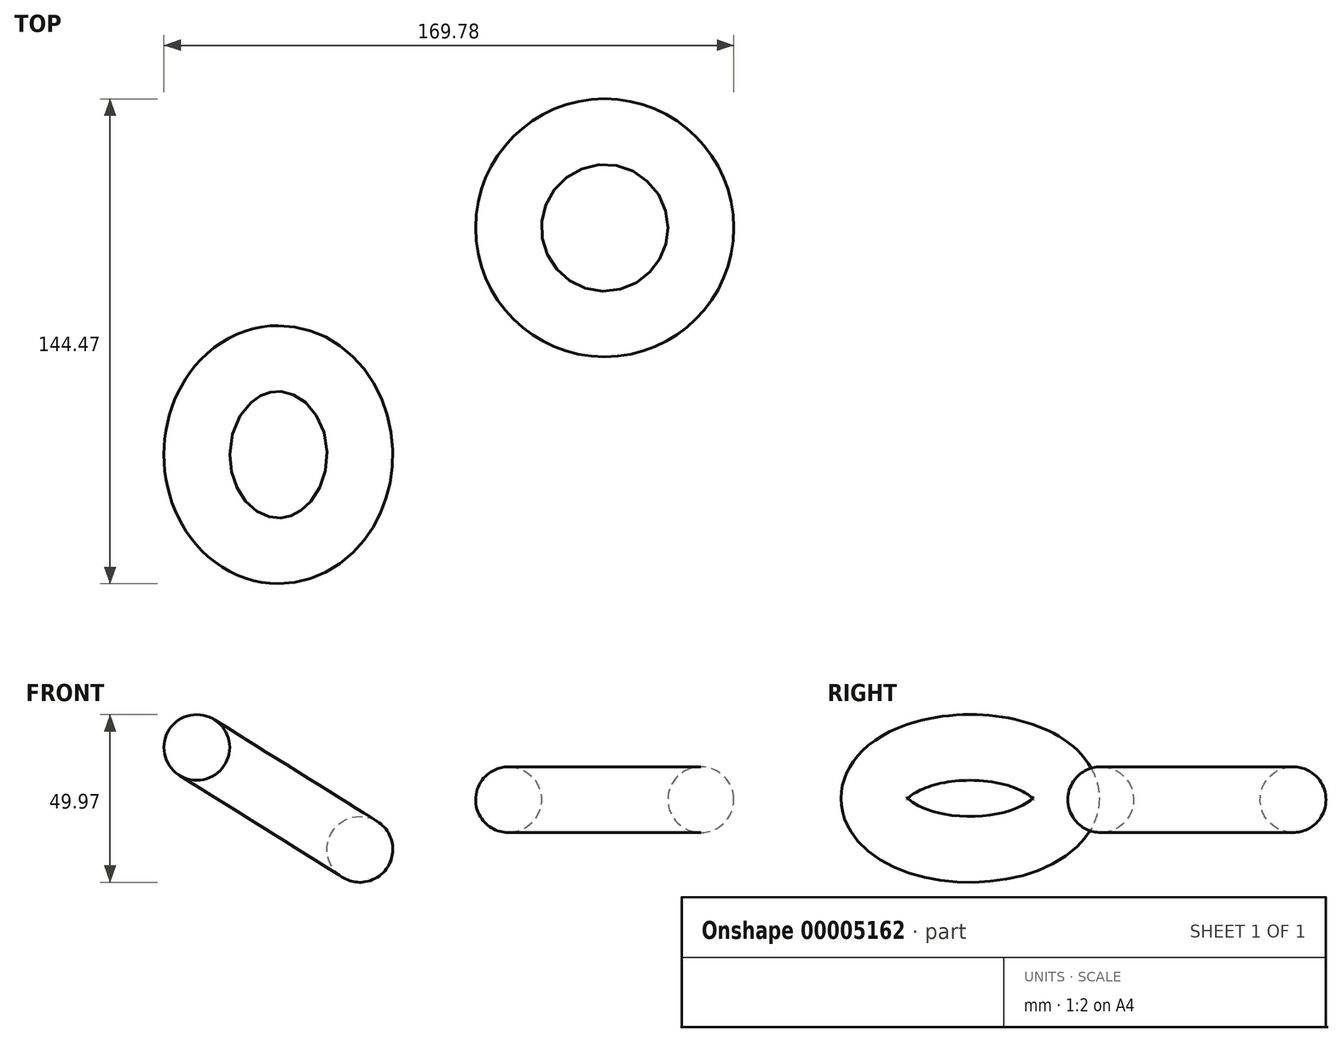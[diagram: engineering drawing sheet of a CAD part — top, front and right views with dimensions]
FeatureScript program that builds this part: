
annotation { "Feature Type Name" : "Feature", "Feature Type Description" : "" }
export const myFeature = defineFeature(function(context is Context, id is Id, definition is map)
    precondition{}
    {
        {
            var Q0;
            Q0=qCreatedBy(makeId("Front.planeOp"),FACE);
            var sketch = newSketch(context, id + "F0", { "sketchPlane" : qUnion([Q0])});
            skCircle(sketch, "E0", {"center": v(0, 0) * mm, "radius": 9.8 * mm});
            skLineSegment(sketch, "E1", {"start": v(-42.15, 28.65) * mm, "end": v(46.2, 28.65) * mm});
            skLineSegment(sketch, "E2", {"start": v(0, 28.65) * mm, "end": v(0, -9.8) * mm});
            skSolve(sketch);
        }
        {
            var Q0;
            Q0=makeQuery(id+"F0.imprint","IMPRINT",FACE,{"disambiguationData":[TD([[makeQuery(id+"F0.imprint","IMPRINT",EDGE,{"derivedFrom":sQuery(id+"F0.wireOp",EDGE,"E0")}),1.0]])]});
            var Q1;
            Q1=sQuery(id+"F0.wireOp",EDGE,"E1");
            revolve(context, id + "F1", {"entities" : qUnion([Q0]), "axis" : qUnion([Q1]), "revolveType" : RevolveType.FULL});
        }
        {
            var Q0;
            Q0=qCreatedBy(makeId("Right.planeOp"),FACE);
            var sketch = newSketch(context, id + "F2", { "sketchPlane" : qUnion([Q0])});
            skLineSegment(sketch, "E3.0", {"start": v(0, -9.8) * mm, "end": v(0, 9.8) * mm});
            skLineSegment(sketch, "E4", {"start": v(0, -9.8) * mm, "end": v(-30.29, -9.8) * mm});
            skSolve(sketch);
        }
        {
            var Q0;
            Q0=makeQuery(id+"F1.opRevolve","SWEPT_BODY",BODY,{"disambiguationData":[OSD([sQuery(id+"F0.wireOp",EDGE,"E0")])]});
            var Q1;
            Q1=sQuery(id+"F2.wireOp",EDGE,"E4");
            transform(context, id + "F3", {"entities" : qUnion([Q0]), "transformType" : TransformType.ROTATION, "transformAxis" : qUnion([Q1]), "angle" : 58 * degree, "makeCopy" : true});
        }
        {
            var Q0;
            Q0=makeQuery(id+"F1.opRevolve","SWEPT_BODY",BODY,{"disambiguationData":[OSD([sQuery(id+"F0.wireOp",EDGE,"E0")])]});
            var Q1;
            Q1=sQuery(id+"F2.wireOp",EDGE,"E4");
            transform(context, id + "F4", {"entities" : qUnion([Q0]), "transformType" : TransformType.ROTATION, "transformAxis" : qUnion([Q1]), "angle" : 270 * degree, "makeCopy" : false});
        }
        {
            var Q0;
            Q0=makeQuery(id+"F1.opRevolve","SWEPT_BODY",BODY,{"disambiguationData":[OSD([sQuery(id+"F0.wireOp",EDGE,"E0")])]});
            transform(context, id + "F5", {"entities" : qUnion([Q0]), "transformType" : TransformType.TRANSLATION_3D, "dx" : 26.17 * mm, "dy" : 67.57 * mm, "dz" : 20 * mm, "makeCopy" : false});
        }
    });
